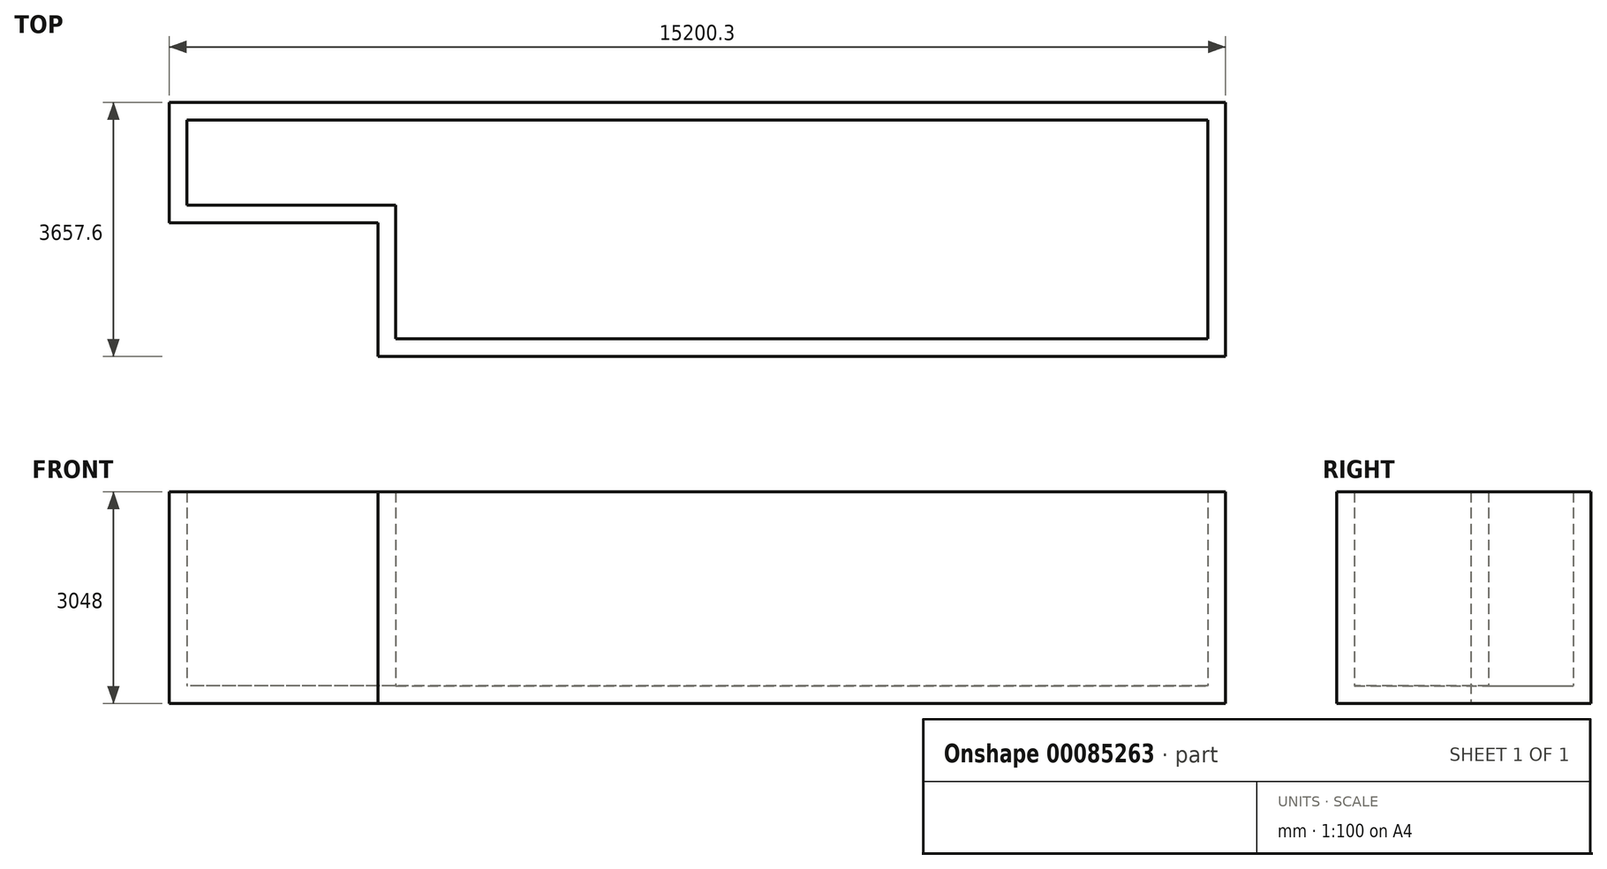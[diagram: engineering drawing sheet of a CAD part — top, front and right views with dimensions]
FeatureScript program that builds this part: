
annotation { "Feature Type Name" : "Feature", "Feature Type Description" : "" }
export const myFeature = defineFeature(function(context is Context, id is Id, definition is map)
    precondition{}
    {
        {
            var Q0;
            Q0=qCreatedBy(makeId("Top.planeOp"),FACE);
            var sketch = newSketch(context, id + "F0", { "sketchPlane" : qUnion([Q0])});
            skLineSegment(sketch, "E0", {"start": v(0, 0) * mm, "end": v(12192, 0) * mm});
            skLineSegment(sketch, "E1", {"start": v(12192, 0) * mm, "end": v(12192, 3657.6) * mm});
            skLineSegment(sketch, "E2", {"start": v(12192, 3657.6) * mm, "end": v(-3008.26, 3657.6) * mm});
            skLineSegment(sketch, "E3", {"start": v(-3008.26, 1927.04) * mm, "end": v(-3008.26, 3657.6) * mm});
            skLineSegment(sketch, "E4", {"start": v(0, 1927.04) * mm, "end": v(-3008.26, 1927.04) * mm});
            skLineSegment(sketch, "E5", {"start": v(0, 1927.04) * mm, "end": v(0, 0) * mm});
            skSolve(sketch);
        }
        {
            var Q0;
            Q0=makeQuery(id+"F0.imprint","IMPRINT",FACE,{"disambiguationData":[TD([[makeQuery(id+"F0.imprint","IMPRINT",EDGE,{"derivedFrom":sQuery(id+"F0.wireOp",EDGE,"E0")}),1.0]])]});
            var Q1;
            Q1 = qConstructionFilter(qBodyType(qCreatedBy(id + "F0" ,EDGE), BodyType.WIRE), ConstructionObject.NO);
            extrude(context, id + "F1", {"entities" : qUnion([Q0]), "surfaceEntities" : qUnion([Q1]), "depth" : 3048 * mm});
        }
        {
            var Q0;
            Q0=makeQuery(id+"F1.opExtrude","CAP_FACE",FACE,{"disambiguationData":[OSD([sQuery(id+"F0.wireOp",EDGE,"E0"),sQuery(id+"F0.wireOp",EDGE,"E1"),sQuery(id+"F0.wireOp",EDGE,"E2"),sQuery(id+"F0.wireOp",EDGE,"E3"),sQuery(id+"F0.wireOp",EDGE,"E4"),sQuery(id+"F0.wireOp",EDGE,"E5")])],"isStart":false});
            shell(context, id + "F2", {"entities" : qUnion([Q0]), "thickness" : 254 * mm});
        }
    });
